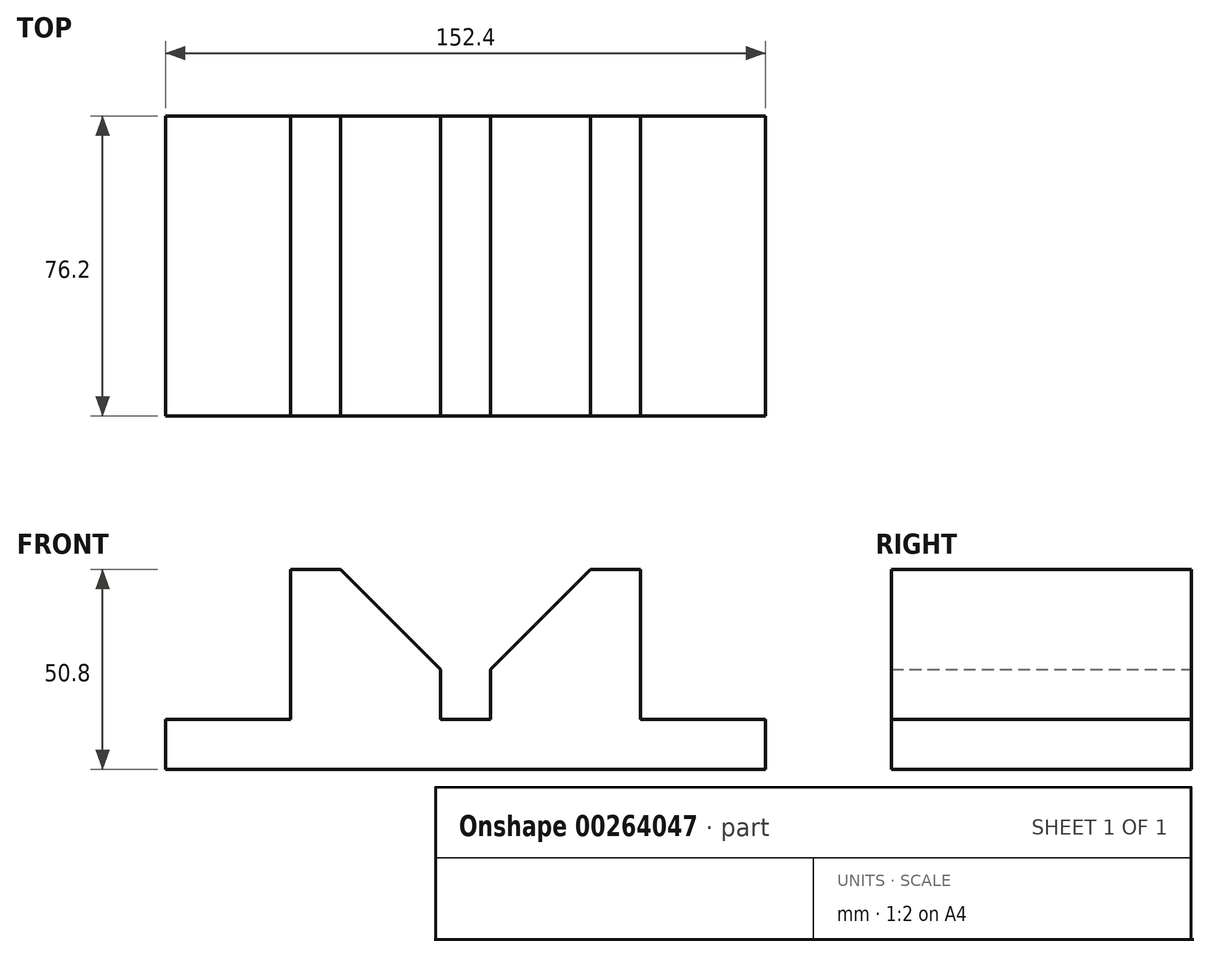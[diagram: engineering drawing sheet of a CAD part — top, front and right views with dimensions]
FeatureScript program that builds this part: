
annotation { "Feature Type Name" : "Feature", "Feature Type Description" : "" }
export const myFeature = defineFeature(function(context is Context, id is Id, definition is map)
    precondition{}
    {
        {
            var Q0;
            Q0=qCreatedBy(makeId("Front.planeOp"),FACE);
            var sketch = newSketch(context, id + "F0", { "sketchPlane" : qUnion([Q0])});
            skLineSegment(sketch, "E0.bottom", {"start": v(-75.84, 12.7) * mm, "end": v(76.56, 12.7) * mm});
            skLineSegment(sketch, "E0.top", {"start": v(-75.84, 0) * mm, "end": v(76.56, 0) * mm});
            skLineSegment(sketch, "E0.left", {"start": v(-75.84, 12.7) * mm, "end": v(-75.84, 0) * mm});
            skLineSegment(sketch, "E0.right", {"start": v(76.56, 12.7) * mm, "end": v(76.56, 0) * mm});
            skLineSegment(sketch, "E1", {"start": v(76.56, 12.7) * mm, "end": v(44.8, 12.7) * mm});
            skLineSegment(sketch, "E2", {"start": v(44.8, 12.7) * mm, "end": v(44.8, 50.8) * mm});
            skLineSegment(sketch, "E3", {"start": v(44.8, 50.8) * mm, "end": v(32.1, 50.8) * mm});
            skLineSegment(sketch, "E4", {"start": v(44.8, 12.7) * mm, "end": v(6.7, 12.7) * mm});
            skLineSegment(sketch, "E5", {"start": v(6.7, 12.7) * mm, "end": v(6.7, 25.4) * mm});
            skLineSegment(sketch, "E6", {"start": v(6.7, 25.4) * mm, "end": v(32.1, 50.8) * mm});
            skLineSegment(sketch, "E7", {"start": v(-75.84, 12.7) * mm, "end": v(-44.1, 12.7) * mm});
            skLineSegment(sketch, "E8", {"start": v(-44.1, 12.7) * mm, "end": v(-44.1, 50.8) * mm});
            skLineSegment(sketch, "E9", {"start": v(-44.1, 50.8) * mm, "end": v(-31.4, 50.8) * mm});
            skLineSegment(sketch, "E10", {"start": v(-44.1, 12.7) * mm, "end": v(-6, 12.7) * mm});
            skLineSegment(sketch, "E11", {"start": v(-6, 12.7) * mm, "end": v(-6, 25.4) * mm});
            skLineSegment(sketch, "E12", {"start": v(-31.4, 50.8) * mm, "end": v(-6, 25.4) * mm});
            skSolve(sketch);
        }
        {
            var Q0;
            Q0 = qSketchRegion(id + "F0", true);
            extrude(context, id + "F1", {"entities" : qUnion([Q0]), "depth" : 76.2 * mm});
        }
    });
